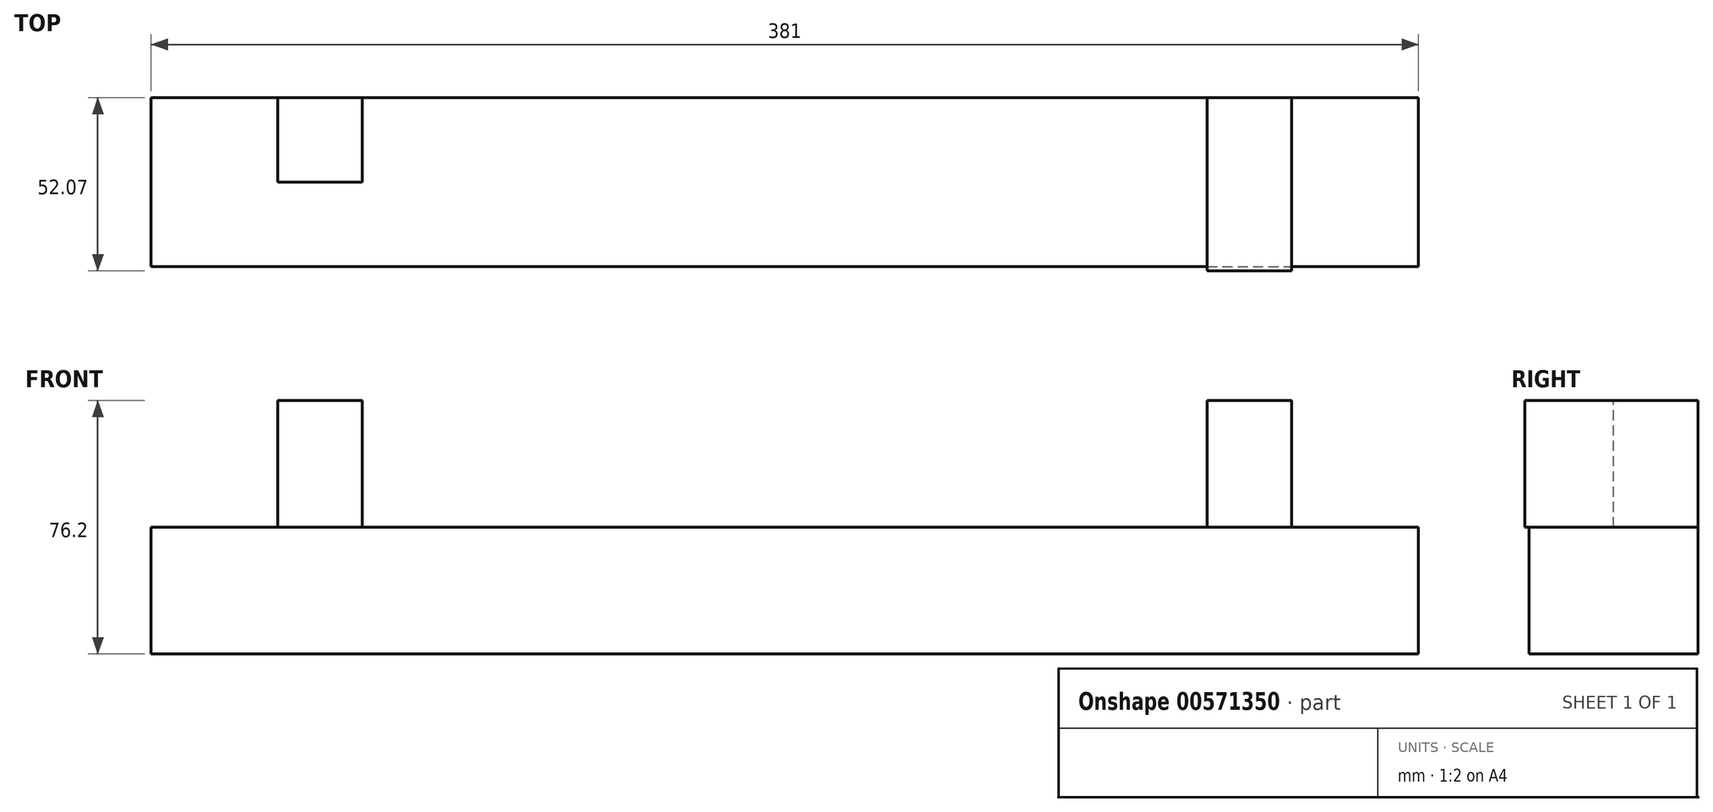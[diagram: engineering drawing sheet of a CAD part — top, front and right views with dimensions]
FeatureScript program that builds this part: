
annotation { "Feature Type Name" : "Feature", "Feature Type Description" : "" }
export const myFeature = defineFeature(function(context is Context, id is Id, definition is map)
    precondition{}
    {
        {
            var Q0;
            Q0=qCreatedBy(makeId("Front.planeOp"),FACE);
            var sketch = newSketch(context, id + "F0", { "sketchPlane" : qUnion([Q0])});
            skLineSegment(sketch, "E0.bottom", {"start": v(-89.01, 38.1) * mm, "end": v(291.99, 38.1) * mm});
            skLineSegment(sketch, "E0.top", {"start": v(-89.01, 0) * mm, "end": v(291.99, 0) * mm});
            skLineSegment(sketch, "E0.left", {"start": v(-89.01, 38.1) * mm, "end": v(-89.01, 0) * mm});
            skLineSegment(sketch, "E0.right", {"start": v(291.99, 38.1) * mm, "end": v(291.99, 0) * mm});
            skLineSegment(sketch, "E1", {"start": v(-50.91, 38.1) * mm, "end": v(-50.91, 76.2) * mm});
            skLineSegment(sketch, "E2", {"start": v(-50.91, 76.2) * mm, "end": v(-25.51, 76.2) * mm});
            skLineSegment(sketch, "E3", {"start": v(-25.51, 76.2) * mm, "end": v(-25.51, 38.1) * mm});
            skLineSegment(sketch, "E4", {"start": v(253.89, 38.1) * mm, "end": v(253.89, 76.2) * mm});
            skLineSegment(sketch, "E5", {"start": v(253.89, 76.2) * mm, "end": v(228.49, 76.2) * mm});
            skLineSegment(sketch, "E6", {"start": v(228.49, 76.2) * mm, "end": v(228.49, 38.1) * mm});
            skSolve(sketch);
        }
        {
            var Q0;
            Q0=makeQuery(id+"F0.imprint","IMPRINT",FACE,{"disambiguationData":[TD([[makeQuery(id+"F0.imprint","IMPRINT",EDGE,{"derivedFrom":sQuery(id+"F0.wireOp",EDGE,"E0.top")}),1.0]])]});
            var Q1;
            {var subQ0=sQuery(id+"F0.wireOp",EDGE,"E4");Q1=makeQuery(id+"F0.imprint","IMPRINT",FACE,{"disambiguationData":[TD([[makeQuery(id+"F0.imprint","IMPRINT",EDGE,{"derivedFrom":subQ0}),1.0]])]});}
            extrude(context, id + "F1", {"entities" : qUnion([Q0, Q1]), "depth" : 50.8 * mm, "offsetDistance" : 25.4 * mm});
        }
        {
            var Q0;
            {var subQ0=sQuery(id+"F0.wireOp",EDGE,"E1");Q0=makeQuery(id+"F0.imprint","IMPRINT",FACE,{"disambiguationData":[TD([[makeQuery(id+"F0.imprint","IMPRINT",EDGE,{"derivedFrom":subQ0}),-1.0]])]});}
            extrude(context, id + "F2", {"entities" : qUnion([Q0]), "operationType" : NewBodyOperationType.ADD, "depth" : 25.4 * mm, "offsetDistance" : 25.4 * mm});
        }
        {
            var Q0;
            Q0=makeQuery(id+"F1.opExtrude","CAP_FACE",FACE,{"disambiguationData":[OSD([sQuery(id+"F0.wireOp",EDGE,"E0.bottom"),sQuery(id+"F0.wireOp",EDGE,"E0.top"),sQuery(id+"F0.wireOp",EDGE,"E0.left"),sQuery(id+"F0.wireOp",EDGE,"E0.right"),sQuery(id+"F0.wireOp",EDGE,"E4"),sQuery(id+"F0.wireOp",EDGE,"E5"),sQuery(id+"F0.wireOp",EDGE,"E6")])],"isStart":false});
            var sketch = newSketch(context, id + "F3", { "sketchPlane" : qUnion([Q0])});
            skLineSegment(sketch, "E7", {"start": v(228.49, 38.1) * mm, "end": v(253.89, 38.1) * mm});
            skSolve(sketch);
        }
        {
            var Q0;
            Q0=makeQuery(id+"F3.imprint","IMPRINT",FACE,{"disambiguationData":[TD([[makeQuery(id+"F3.imprint","IMPRINT",EDGE,{"derivedFrom":sQuery(id+"F3.wireOp",EDGE,"E7")}),1.0]])]});
            extrude(context, id + "F4", {"entities" : qUnion([Q0]), "operationType" : NewBodyOperationType.ADD, "depth" : 1.27 * mm, "offsetDistance" : 25.4 * mm});
        }
    });
